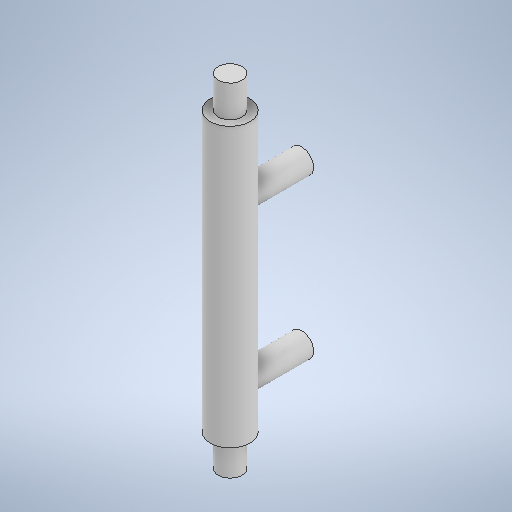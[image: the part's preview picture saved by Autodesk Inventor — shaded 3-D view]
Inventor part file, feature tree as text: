
AUTODESK INVENTOR PART (.ipt)
format: ipt  version: 2025.1 (Build 291241000, 241)  size: 280,576 bytes
history: native  units: mm
features: extrude x4, sketch x4, plane x1
ambient origin geometry x8: Origin, YZ Plane, XZ Plane, XY Plane, X Axis, Y Axis, Z Axis, Center Point
bodies: Solid1 (feature_tree)
feature tree (9):
  extrude  "Extrusion1"  Depth=10.0mm TaperAngle=0.0deg
  extrude  "Extrusion2"  Depth=8.0mm TaperAngle=0.0deg
  extrude  "Extrusion3"  Depth=8.0mm TaperAngle=0.0deg
  plane  "Work Plane1"
  extrude  "Extrusion4"  Depth=10.0mm
  sketch  "Sketch1"  dims[d0=10.0mm d1=70.0mm d2=0.0mm]
  sketch  "Sketch2"  dims[d3=6.0mm d4=8.0mm d5=0.0mm]
  sketch  "Sketch3"  dims[d6=6.0mm d7=8.0mm d8=0.0mm]
  sketch  "Sketch4"  dims[d9=18.0mm d10=6.0mm d11=6.0mm d12=40.0mm d13=10.0mm d14=8.0mm d15=0.0mm]
